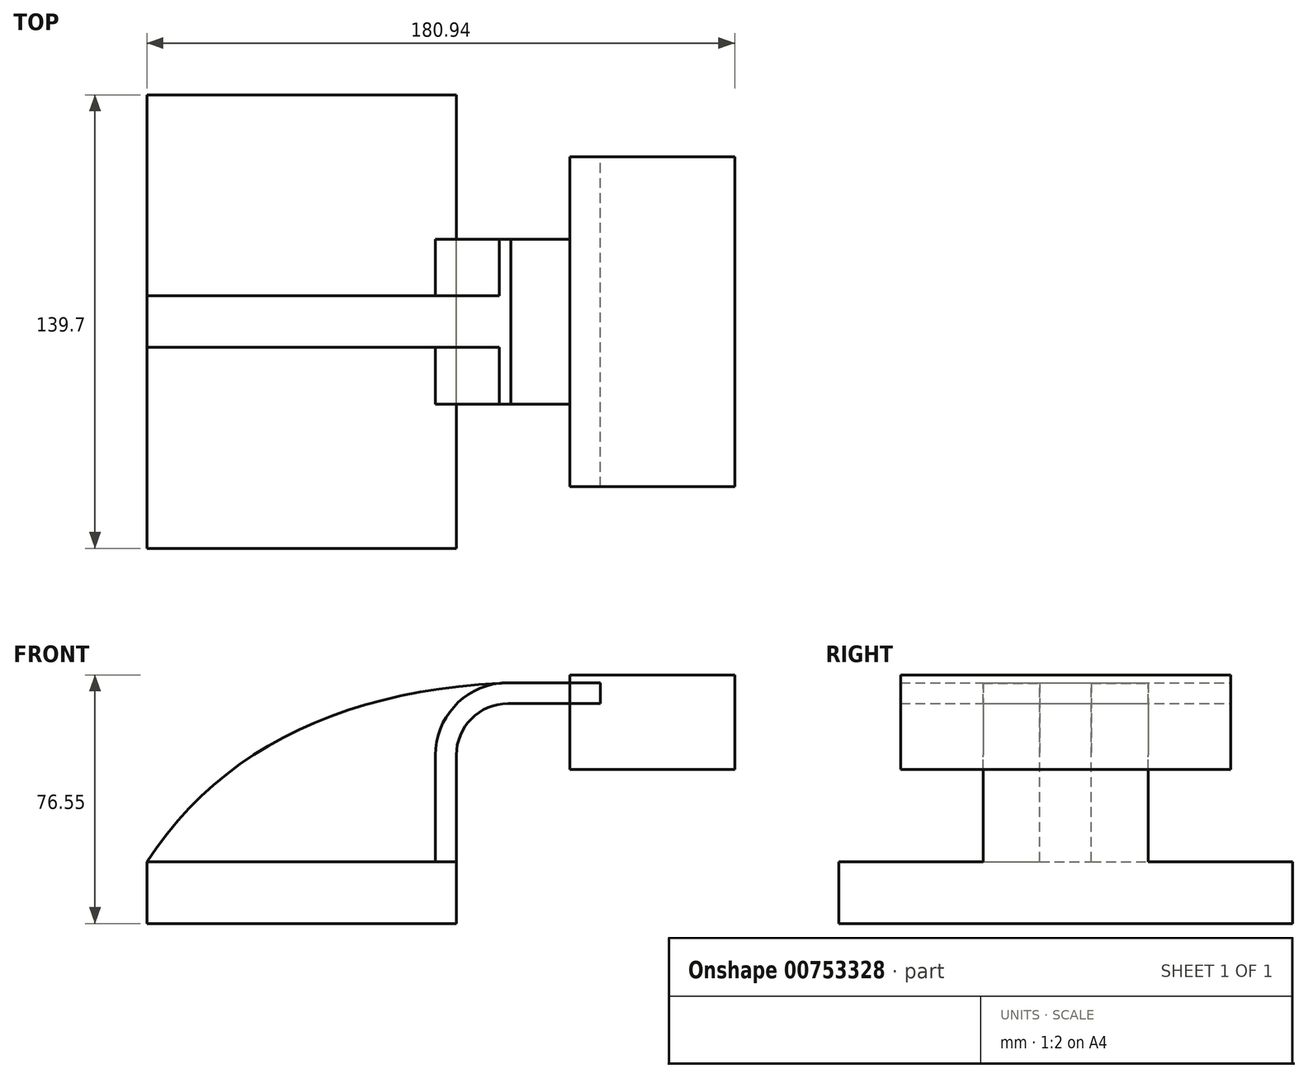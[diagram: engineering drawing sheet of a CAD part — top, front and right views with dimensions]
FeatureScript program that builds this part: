
annotation { "Feature Type Name" : "Feature", "Feature Type Description" : "" }
export const myFeature = defineFeature(function(context is Context, id is Id, definition is map)
    precondition{}
    {
        {
            var Q0;
            Q0=qCreatedBy(makeId("Front.planeOp"),FACE);
            var sketch = newSketch(context, id + "F0", { "sketchPlane" : qUnion([Q0])});
            skLineSegment(sketch, "E0.bottom", {"start": v(-47.63, -9.53) * mm, "end": v(47.63, -9.53) * mm});
            skLineSegment(sketch, "E0.top", {"start": v(-47.63, 9.52) * mm, "end": v(47.63, 9.52) * mm});
            skLineSegment(sketch, "E0.left", {"start": v(-47.63, -9.53) * mm, "end": v(-47.63, 9.52) * mm});
            skLineSegment(sketch, "E0.right", {"start": v(47.63, -9.53) * mm, "end": v(47.63, 9.52) * mm});
            skPoint(sketch, "E0.middle", {"position": v(0, 0) * mm});
            skLineSegment(sketch, "E1.bottom", {"start": v(82.5, 37.94) * mm, "end": v(133.3, 37.94) * mm});
            skLineSegment(sketch, "E1.top", {"start": v(82.5, 67.02) * mm, "end": v(133.3, 67.02) * mm});
            skLineSegment(sketch, "E1.left", {"start": v(82.5, 37.94) * mm, "end": v(82.5, 67.02) * mm});
            skLineSegment(sketch, "E1.right", {"start": v(133.3, 37.94) * mm, "end": v(133.3, 67.02) * mm});
            skPoint(sketch, "E1.middle", {"position": v(107.9, 52.48) * mm});
            skLineSegment(sketch, "E2", {"start": v(47.63, 9.52) * mm, "end": v(47.63, 42.34) * mm});
            skArc(sketch, "E3", {"start": v(47.62, 42.34) * mm, "mid": v(52.27, 53.57) * mm, "end": v(63.5, 58.22) * mm});
            skLineSegment(sketch, "E4", {"start": v(63.5, 58.22) * mm, "end": v(91.92, 58.22) * mm});
            skLineSegment(sketch, "E5.0", {"start": v(63.5, 64.64) * mm, "end": v(91.92, 64.64) * mm});
            skArc(sketch, "E5.1", {"start": v(41.2, 42.34) * mm, "mid": v(47.73, 58.11) * mm, "end": v(63.5, 64.64) * mm});
            skLineSegment(sketch, "E5.2", {"start": v(41.2, 9.52) * mm, "end": v(41.2, 42.34) * mm});
            skLineSegment(sketch, "E6", {"start": v(91.92, 64.64) * mm, "end": v(91.92, 58.22) * mm});
            skPoint(sketch, "E7.1.internal.snap0", {"position": v(77.71, 64.64) * mm});
            skFitSpline(sketch, "E7", {"points": [v(-47.63, 9.53) * mm, v(82.5, 64.64) * mm], "startDerivative": vector(76.87, 118) * mm, "endDerivative": vector(179.09, -6.23) * mm});
            skSolve(sketch);
        }
        {
            var Q0;
            Q0=makeQuery(id+"F0.imprint","IMPRINT",FACE,{"disambiguationData":[TD([[makeQuery(id+"F0.imprint","IMPRINT",EDGE,{"derivedFrom":sQuery(id+"F0.wireOp",EDGE,"E0.bottom")}),1.0]])]});
            extrude(context, id + "F1", {"entities" : qUnion([Q0]), "endBound" : BoundingType.SYMMETRIC, "depth" : 139.7 * mm, "offsetDistance" : 25.4 * mm});
        }
        {
            var Q0;
            {var subQ3=sQuery(id+"F0.wireOp",EDGE,"E5.2");Q0=makeQuery(id+"F0.imprint","IMPRINT",FACE,{"disambiguationData":[TD([[makeQuery(id+"F0.imprint","IMPRINT",EDGE,{"derivedFrom":subQ3}),1.0]])]});}
            extrude(context, id + "F2", {"entities" : qUnion([Q0]), "operationType" : NewBodyOperationType.ADD, "endBound" : BoundingType.SYMMETRIC, "depth" : 15.88 * mm, "offsetDistance" : 25.4 * mm});
        }
        {
            var Q0;
            {var subQ0=sQuery(id+"F0.wireOp",EDGE,"E2");Q0=makeQuery(id+"F0.imprint","IMPRINT",FACE,{"disambiguationData":[TD([[makeQuery(id+"F0.imprint","IMPRINT",EDGE,{"derivedFrom":subQ0}),1.0]])]});}
            extrude(context, id + "F3", {"entities" : qUnion([Q0]), "operationType" : NewBodyOperationType.ADD, "endBound" : BoundingType.SYMMETRIC, "depth" : 50.8 * mm, "offsetDistance" : 25.4 * mm});
        }
        {
            var Q0;
            {var subQ4=sQuery(id+"F0.wireOp",EDGE,"E1.bottom");Q0=makeQuery(id+"F0.imprint","IMPRINT",FACE,{"disambiguationData":[TD([[makeQuery(id+"F0.imprint","IMPRINT",EDGE,{"derivedFrom":subQ4}),1.0]])]});}
            extrude(context, id + "F4", {"entities" : qUnion([Q0]), "endBound" : BoundingType.SYMMETRIC, "depth" : 101.6 * mm, "offsetDistance" : 25.4 * mm});
        }
    });
